# Revit family: TV
name_source: partatom
category: Electrical Fixtures
units: mm (PartAtom-declared; Revit-internal decimal feet)

## family parameters
Always vertical = No
Cut with Voids When Loaded = No
Maintain Annotation Orientation = Yes
Part Type = Normal
Room Calculation Point = No
Round Connector Dimension = Use Diameter
Shared = Yes
Work Plane-Based = Yes

## types (1)
- TV
    ANCHO RECEPTACULO = 36 mm  [stored 0.11811 ft]
    Default Elevation = 1219 mm
    ESPESOR = 8 mm  [stored 0.0262467 ft]
    ESPESOR BASE = 3 mm  [stored 0.00984252 ft]
    ET = 2 mm  [stored 0.00656168 ft]
    INCLUIR EN LISTADO = No
    LARGO CONECTOR = 10 mm  [stored 0.0328084 ft]
    LONGITUD RECEPTACULO = 65 mm  [stored 0.213255 ft]
    MATERIAL 3 = Acero Niquelado
    PROFUNDIDAD RANURA = 10 mm  [stored 0.0328084 ft]
    RC = 1 mm  [stored 0.00328084 ft]

note: [stored X ft] marks values corroborated as IEEE doubles in the binary element streams (Revit-internal decimal feet)

## geometry (parser evidence)
native form markers: Sweep x4
no freeform markers — native parametric forms only
